# Revit family: IEK_Зажим соединительный параллельный_Полоса-пруток-полоса-пруток_Пруток_Соединение
name_source: partatom
category: Соединительные детали воздуховодов
units: mm (PartAtom-declared; Revit-internal decimal feet)

## family parameters
Всегда вертикально = Да
На основе рабочей плоскости = Нет
Общий = Нет
При загрузке вырезать с полостями = Нет
Размер круглого соединителя = Использовать диаметр
Тип детали = Соединение

## types (2) — shared parameters
ADSK_URL страницы изделия = https://www.iek.ru
ADSK_Версия Revit = 2019
ADSK_Версия семейства = 1.0
ADSK_Группирование = VIII. ЭЛЕМЕНТЫ ВНЕШНЕЙ МОЛНИЕЗАЩИТЫ
ADSK_Единица измерения = шт
ADSK_Завод-изготовитель = IEK
ADSK_Масса = 0.13
IEK_URL = https://www.iek.ru
IEK_Описание = Зажим соединительный параллельный полоса/пруток – полоса/пруток товарного знака IEK используется для соединения плоских или круглых проводников параллельным способом. Наличие разделительной пластины позволяет предотвратить контактную коррозию в воздухе между металлами.

## per-type parameters (varying)
| type | ADSK_Код изделия | ADSK_Материал | ADSK_Материал наименование | ADSK_Наименование | IEK_Цена за единицу | KSI_CMa_Строительные материалы |
| 20-40_8-10_Сталь нержавеющая | ZCC14-20-1-16-40 | Сталь нержавеющая | Сталь нержавеющая | Зажим соед. паралл. пол./прут.—пол./прут. нерж. сталь IEK | 1100 | СТ 10 02 10 40 |
| 20-40_8-10_Сталь оцинкованная | ZCC14-11-1-16-40 | Сталь оцинкованная | Сталь оцинкованная | Зажим соед. параллельный пол./прут.—пол. оц. сталь IEK | 510 | 24.10.35.000.08.3.05.06-0001 |
